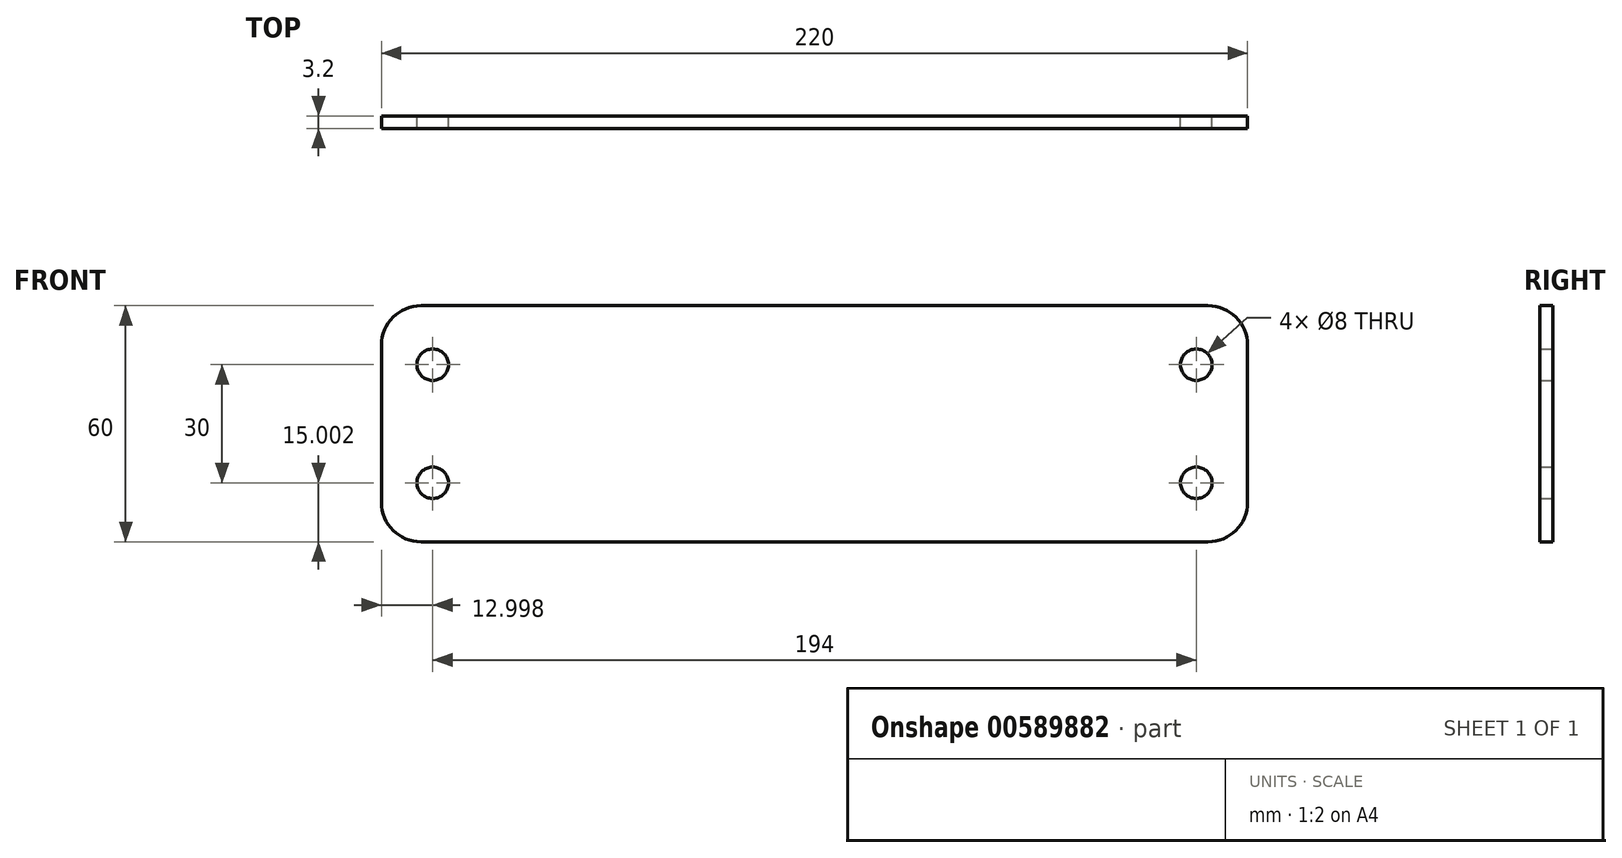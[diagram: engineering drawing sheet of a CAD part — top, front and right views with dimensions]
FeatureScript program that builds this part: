
annotation { "Feature Type Name" : "Feature", "Feature Type Description" : "" }
export const myFeature = defineFeature(function(context is Context, id is Id, definition is map)
    precondition{}
    {
        {
            var Q0;
            Q0=qCreatedBy(makeId("Top.planeOp"),FACE);
            var sketch = newSketch(context, id + "F0", { "sketchPlane" : qUnion([Q0])});
            skLineSegment(sketch, "E0", {"start": v(-60.77, -19.8) * mm, "end": v(-32.77, -19.8) * mm});
            skLineSegment(sketch, "E1", {"start": v(-30.77, -17.8) * mm, "end": v(-30.77, 18.2) * mm});
            skLineSegment(sketch, "E2", {"start": v(-28.77, 20.2) * mm, "end": v(47.23, 20.2) * mm});
            skLineSegment(sketch, "E3", {"start": v(49.23, 18.2) * mm, "end": v(49.23, -17.8) * mm});
            skLineSegment(sketch, "E4", {"start": v(51.23, -19.8) * mm, "end": v(79.23, -19.8) * mm});
            skLineSegment(sketch, "E5.0", {"start": v(54.23, -16.8) * mm, "end": v(79.23, -16.8) * mm});
            skLineSegment(sketch, "E5.1", {"start": v(-60.77, -16.8) * mm, "end": v(-35.77, -16.8) * mm});
            skLineSegment(sketch, "E5.2", {"start": v(-33.77, -14.8) * mm, "end": v(-33.77, 23.2) * mm});
            skLineSegment(sketch, "E5.3", {"start": v(-33.77, 23.2) * mm, "end": v(50.23, 23.2) * mm});
            skLineSegment(sketch, "E5.4", {"start": v(52.23, 21.2) * mm, "end": v(52.23, -14.8) * mm});
            skLineSegment(sketch, "E6", {"start": v(-60.77, -19.8) * mm, "end": v(-60.77, -16.8) * mm});
            skLineSegment(sketch, "E7", {"start": v(79.23, -19.8) * mm, "end": v(79.23, -16.8) * mm});
            skLineSegment(sketch, "E8", {"start": v(-32.58, 23.2) * mm, "end": v(-33.77, 21.59) * mm});
            skPoint(sketch, "E9.visualSharp", {"position": v(52.23, 23.2) * mm});
            skArc(sketch, "E9.filletArc", {"start": v(52.23, 21.2) * mm, "mid": v(51.64, 22.6) * mm, "end": v(50.23, 23.2) * mm});
            skPoint(sketch, "E10.visualSharp", {"position": v(49.23, 20.2) * mm});
            skArc(sketch, "E10.filletArc", {"start": v(49.23, 18.2) * mm, "mid": v(48.64, 19.6) * mm, "end": v(47.23, 20.2) * mm});
            skPoint(sketch, "E11.visualSharp", {"position": v(-30.77, 20.2) * mm});
            skArc(sketch, "E11.filletArc", {"start": v(-28.77, 20.2) * mm, "mid": v(-30.18, 19.6) * mm, "end": v(-30.77, 18.2) * mm});
            skPoint(sketch, "E12.visualSharp", {"position": v(-33.77, -16.8) * mm});
            skArc(sketch, "E12.filletArc", {"start": v(-35.77, -16.8) * mm, "mid": v(-34.36, -16.22) * mm, "end": v(-33.77, -14.8) * mm});
            skPoint(sketch, "E13.visualSharp", {"position": v(-30.77, -19.8) * mm});
            skArc(sketch, "E13.filletArc", {"start": v(-32.77, -19.8) * mm, "mid": v(-31.36, -19.22) * mm, "end": v(-30.77, -17.8) * mm});
            skPoint(sketch, "E14.visualSharp", {"position": v(49.23, -19.8) * mm});
            skArc(sketch, "E14.filletArc", {"start": v(49.23, -17.8) * mm, "mid": v(49.82, -19.22) * mm, "end": v(51.23, -19.8) * mm});
            skPoint(sketch, "E15.visualSharp", {"position": v(52.23, -16.8) * mm});
            skArc(sketch, "E15.filletArc", {"start": v(52.23, -14.8) * mm, "mid": v(52.82, -16.22) * mm, "end": v(54.23, -16.8) * mm});
            skSolve(sketch);
        }
        {
            var Q0;
            Q0=qCreatedBy(makeId("Front.planeOp"),FACE);
            cPlane(context, id + "F1", {"entities" : qUnion([Q0]), "cplaneType" : CPlaneType.OFFSET, "offset" : 21 * mm, "width" : 150 * mm, "height" : 150 * mm});
        }
        {
            var Q0;
            Q0=qCreatedBy(id+"F1.planeOp",FACE);
            var sketch = newSketch(context, id + "F2", { "sketchPlane" : qUnion([Q0])});
            skLineSegment(sketch, "E16.bottom", {"start": v(-279.65, 60.32) * mm, "end": v(-184.46, 60.32) * mm});
            skLineSegment(sketch, "E16.top", {"start": v(-279.65, 0.32) * mm, "end": v(-79.65, 0.32) * mm});
            skLineSegment(sketch, "E16.left", {"start": v(-289.65, 50.32) * mm, "end": v(-289.65, 10.32) * mm});
            skLineSegment(sketch, "E16.right", {"start": v(-69.65, 50.32) * mm, "end": v(-69.65, 10.32) * mm});
            skPoint(sketch, "E17.visualSharp", {"position": v(-289.65, 60.32) * mm});
            skArc(sketch, "E17.filletArc", {"start": v(-279.65, 60.32) * mm, "mid": v(-286.72, 57.4) * mm, "end": v(-289.65, 50.32) * mm});
            skPoint(sketch, "E18.visualSharp", {"position": v(-289.65, 0.32) * mm});
            skArc(sketch, "E18.filletArc", {"start": v(-289.65, 10.32) * mm, "mid": v(-286.72, 3.25) * mm, "end": v(-279.65, 0.32) * mm});
            skPoint(sketch, "E19.visualSharp", {"position": v(-69.65, 0.32) * mm});
            skArc(sketch, "E19.filletArc", {"start": v(-79.65, 0.32) * mm, "mid": v(-72.58, 3.25) * mm, "end": v(-69.65, 10.32) * mm});
            skPoint(sketch, "E20.visualSharp", {"position": v(-69.65, 60.32) * mm});
            skArc(sketch, "E20.filletArc", {"start": v(-69.65, 50.32) * mm, "mid": v(-72.58, 57.4) * mm, "end": v(-79.65, 60.32) * mm});
            skCircle(sketch, "E21", {"center": v(-276.65, 45.32) * mm, "radius": 4 * mm});
            skCircle(sketch, "E22", {"center": v(-276.65, 15.32) * mm, "radius": 4 * mm});
            skCircle(sketch, "E23", {"center": v(-82.65, 15.32) * mm, "radius": 4 * mm});
            skCircle(sketch, "E24", {"center": v(-82.65, 45.32) * mm, "radius": 4 * mm});
            skLineSegment(sketch, "E25.trimOffspring", {"start": v(-104.46, 60.32) * mm, "end": v(-79.65, 60.32) * mm});
            skLineSegment(sketch, "E26", {"start": v(-184.46, 60.32) * mm, "end": v(-104.46, 60.32) * mm});
            skSolve(sketch);
        }
        {
            var Q0;
            Q0=qSketchRegion(id+"F2",true);
            extrude(context, id + "F3", {"entities" : qUnion([Q0]), "depth" : 3.2 * mm, "offsetDistance" : 25 * mm});
        }
    });
